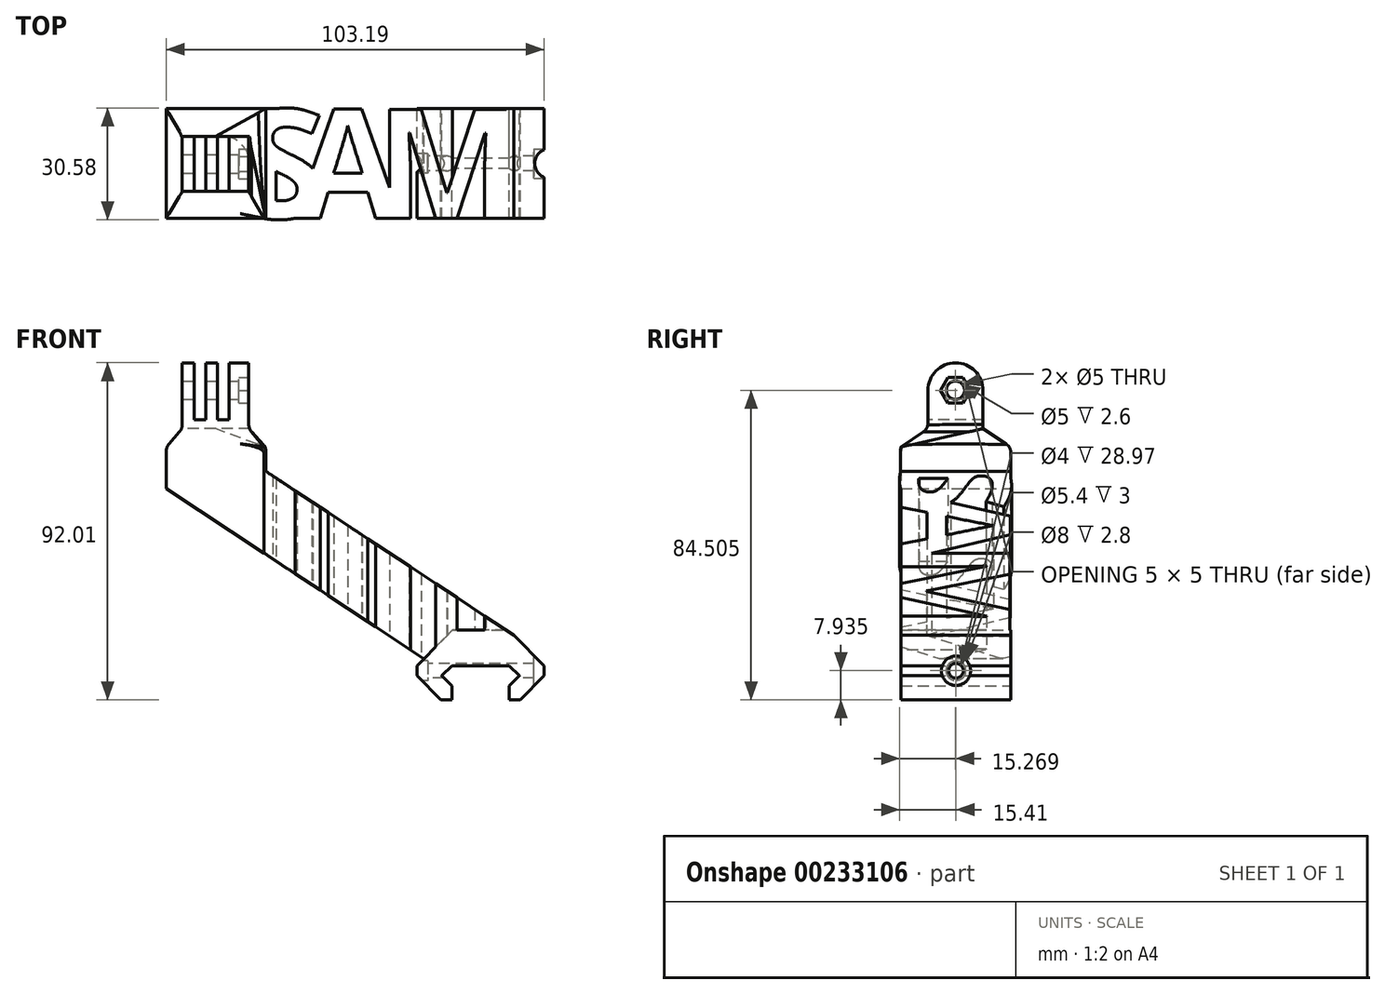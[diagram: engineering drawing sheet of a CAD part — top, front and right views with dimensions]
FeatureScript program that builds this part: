
annotation { "Feature Type Name" : "Feature", "Feature Type Description" : "" }
export const myFeature = defineFeature(function(context is Context, id is Id, definition is map)
    precondition{}
    {
        {
            var Q0;
            Q0=qCreatedBy(makeId("Front.planeOp"),FACE);
            var sketch = newSketch(context, id + "F0", { "sketchPlane" : qUnion([Q0])});
            skLineSegment(sketch, "E0", {"start": v(0, 0) * mm, "end": v(-7.83, 0) * mm, "construction": true});
            skLineSegment(sketch, "E1", {"start": v(-7.83, 0) * mm, "end": v(-7.83, 3.78) * mm});
            skLineSegment(sketch, "E2", {"start": v(-7.84, 3.78) * mm, "end": v(-10.6, 6.55) * mm});
            skLineSegment(sketch, "E3", {"start": v(-10.6, 6.55) * mm, "end": v(-7.83, 9.32) * mm});
            skLineSegment(sketch, "E4", {"start": v(-7.84, 9.32) * mm, "end": v(0, 9.32) * mm});
            skLineSegment(sketch, "E5", {"start": v(0, 9.32) * mm, "end": v(0, 0) * mm, "construction": true});
            skLineSegment(sketch, "E6", {"start": v(-7.83, 9.32) * mm, "end": v(-7.83, 3.78) * mm, "construction": true});
            skLineSegment(sketch, "E7.MirrorCS", {"start": v(7.84, 9.32) * mm, "end": v(0, 9.32) * mm});
            skLineSegment(sketch, "E8.MirrorCS", {"start": v(10.6, 6.55) * mm, "end": v(7.83, 9.32) * mm});
            skLineSegment(sketch, "E9.MirrorCS", {"start": v(7.84, 3.78) * mm, "end": v(10.6, 6.55) * mm});
            skLineSegment(sketch, "E10.MirrorCS", {"start": v(7.83, 0) * mm, "end": v(7.83, 3.78) * mm});
            skLineSegment(sketch, "E11", {"start": v(-10.84, 0) * mm, "end": v(-17.38, 6.55) * mm});
            skLineSegment(sketch, "E12", {"start": v(-17.38, 6.55) * mm, "end": v(-17.38, 9.32) * mm});
            skLineSegment(sketch, "E13", {"start": v(-17.39, 9.32) * mm, "end": v(-7.7, 19) * mm});
            skLineSegment(sketch, "E14", {"start": v(-7.7, 19) * mm, "end": v(0, 19) * mm});
            skLineSegment(sketch, "E15", {"start": v(-10.6, 6.55) * mm, "end": v(-17.38, 6.55) * mm, "construction": true});
            skLineSegment(sketch, "E16", {"start": v(-17.38, 9.32) * mm, "end": v(-7.84, 9.32) * mm, "construction": true});
            skLineSegment(sketch, "E17.MirrorCS", {"start": v(7.7, 19) * mm, "end": v(0, 19) * mm});
            skLineSegment(sketch, "E18.MirrorCS", {"start": v(17.39, 9.32) * mm, "end": v(7.7, 19) * mm});
            skLineSegment(sketch, "E19.MirrorCS", {"start": v(17.38, 6.55) * mm, "end": v(17.38, 9.32) * mm});
            skLineSegment(sketch, "E20.MirrorCS", {"start": v(10.83, 0) * mm, "end": v(17.38, 6.55) * mm});
            skLineSegment(sketch, "E21", {"start": v(-7.83, 0) * mm, "end": v(-10.84, 0) * mm});
            skLineSegment(sketch, "E22", {"start": v(7.83, 0) * mm, "end": v(10.84, 0) * mm});
            skSolve(sketch);
        }
        {
            var Q0;
            Q0=makeQuery(id+"F0.imprint","IMPRINT",FACE,{"disambiguationData":[TD([[makeQuery(id+"F0.imprint","IMPRINT",EDGE,{"derivedFrom":sQuery(id+"F0.wireOp",EDGE,"E1")}),1.0]])]});
            extrude(context, id + "F1", {"entities" : qUnion([Q0]), "depth" : 30 * mm, "offsetDistance" : 25 * mm});
        }
        {
            var Q0;
            Q0=makeQuery(id+"F1.opExtrude","SWEPT_FACE",FACE,{"disambiguationData":[OSD([sQuery(id+"F0.wireOp",EDGE,"E12")])]});
            var sketch = newSketch(context, id + "F2", { "sketchPlane" : qUnion([Q0])});
            skCircle(sketch, "E23", {"center": v(15, 7.94) * mm, "radius": 2 * mm});
            skPoint(sketch, "E23.centerSnap0", {"position": v(15, 6.55) * mm});
            skLineSegment(sketch, "E24", {"start": v(15, 9.32) * mm, "end": v(15, 6.55) * mm, "construction": true});
            skSolve(sketch);
        }
        {
            var Q0;
            Q0=qSketchRegion(id+"F2",true);
            extrude(context, id + "F3", {"entities" : qUnion([Q0]), "operationType" : NewBodyOperationType.REMOVE, "oppositeDirection" : true, "depth" : 61.1 * mm, "offsetDistance" : 25 * mm});
        }
        {
            var Q0;
            {var subQ0=sQuery(id+"F0.wireOp",EDGE,"E13");var subQ1=sQuery(id+"F0.wireOp",EDGE,"E12");var subQ2=sQuery(id+"F0.wireOp",EDGE,"E11");Q0=makeQuery(id+"F3.boolean.opBoolean","SPLIT",FACE,{"disambiguationData":[TD([makeQuery(id+"F1.opExtrude","CAP_FACE",FACE,{"disambiguationData":[OSD([sQuery(id+"F0.wireOp",EDGE,"E1"),sQuery(id+"F0.wireOp",EDGE,"E2"),sQuery(id+"F0.wireOp",EDGE,"E3"),sQuery(id+"F0.wireOp",EDGE,"E4"),sQuery(id+"F0.wireOp",EDGE,"E7.MirrorCS"),sQuery(id+"F0.wireOp",EDGE,"E8.MirrorCS"),sQuery(id+"F0.wireOp",EDGE,"E9.MirrorCS"),sQuery(id+"F0.wireOp",EDGE,"E10.MirrorCS"),subQ2,subQ1,subQ0,sQuery(id+"F0.wireOp",EDGE,"E14"),sQuery(id+"F0.wireOp",EDGE,"E17.MirrorCS"),sQuery(id+"F0.wireOp",EDGE,"E18.MirrorCS"),sQuery(id+"F0.wireOp",EDGE,"E19.MirrorCS"),sQuery(id+"F0.wireOp",EDGE,"E20.MirrorCS"),sQuery(id+"F0.wireOp",EDGE,"E21"),sQuery(id+"F0.wireOp",EDGE,"E22")])],"isStart":false})])],"derivedFrom":makeQuery(id+"F1.opExtrude","SWEPT_FACE",FACE,{"disambiguationData":[OSD([subQ1])]})});}
            var sketch = newSketch(context, id + "F4", { "sketchPlane" : qUnion([Q0])});
            skCircle(sketch, "E25", {"center": v(15, 7.94) * mm, "radius": 2.7 * mm});
            skSolve(sketch);
        }
        {
            var Q0;
            Q0=qSketchRegion(id+"F4",true);
            extrude(context, id + "F5", {"entities" : qUnion([Q0]), "operationType" : NewBodyOperationType.REMOVE, "oppositeDirection" : true, "depth" : 3 * mm, "offsetDistance" : 25 * mm});
        }
        {
            var Q0;
            {var subQ0=sQuery(id+"F0.wireOp",EDGE,"E20.MirrorCS");var subQ1=sQuery(id+"F0.wireOp",EDGE,"E19.MirrorCS");var subQ2=sQuery(id+"F0.wireOp",EDGE,"E18.MirrorCS");Q0=makeQuery(id+"F3.boolean.opBoolean","SPLIT",FACE,{"disambiguationData":[TD([makeQuery(id+"F1.opExtrude","CAP_FACE",FACE,{"disambiguationData":[OSD([sQuery(id+"F0.wireOp",EDGE,"E1"),sQuery(id+"F0.wireOp",EDGE,"E2"),sQuery(id+"F0.wireOp",EDGE,"E3"),sQuery(id+"F0.wireOp",EDGE,"E4"),sQuery(id+"F0.wireOp",EDGE,"E7.MirrorCS"),sQuery(id+"F0.wireOp",EDGE,"E8.MirrorCS"),sQuery(id+"F0.wireOp",EDGE,"E9.MirrorCS"),sQuery(id+"F0.wireOp",EDGE,"E10.MirrorCS"),sQuery(id+"F0.wireOp",EDGE,"E11"),sQuery(id+"F0.wireOp",EDGE,"E12"),sQuery(id+"F0.wireOp",EDGE,"E13"),sQuery(id+"F0.wireOp",EDGE,"E14"),sQuery(id+"F0.wireOp",EDGE,"E17.MirrorCS"),subQ2,subQ1,subQ0,sQuery(id+"F0.wireOp",EDGE,"E21"),sQuery(id+"F0.wireOp",EDGE,"E22")])],"isStart":false})])],"derivedFrom":makeQuery(id+"F1.opExtrude","SWEPT_FACE",FACE,{"disambiguationData":[OSD([subQ1])]})});}
            var sketch = newSketch(context, id + "F6", { "sketchPlane" : qUnion([Q0])});
            skCircle(sketch, "E26", {"center": v(-15, 7.93) * mm, "radius": 4 * mm});
            skSolve(sketch);
        }
        {
            var Q0;
            Q0=qSketchRegion(id+"F6",true);
            extrude(context, id + "F7", {"entities" : qUnion([Q0]), "operationType" : NewBodyOperationType.REMOVE, "oppositeDirection" : true, "depth" : 2.8 * mm, "offsetDistance" : 25 * mm});
        }
        {
            var Q0;
            Q0=makeQuery(id+"F1.opExtrude","SWEPT_FACE",FACE,{"disambiguationData":[OSD([sQuery(id+"F0.wireOp",EDGE,"E14"),sQuery(id+"F0.wireOp",EDGE,"E17.MirrorCS")])]});
            var sketch = newSketch(context, id + "F8", { "sketchPlane" : qUnion([Q0])});
            skText(sketch, "E27", { "text": "M", "fontName": "OpenSans-Bold.ttf"});
            skText(sketch, "E28", { "text": "A", "fontName": "OpenSans-Bold.ttf"});
            skText(sketch, "E29", { "text": "S", "fontName": "OpenSans-Bold.ttf"});
            skLineSegment(sketch, "E30.bottom", {"start": v(-55.8, -30) * mm, "end": v(-85.8, -30) * mm});
            skLineSegment(sketch, "E30.top", {"start": v(-55.8, 0) * mm, "end": v(-85.8, 0) * mm});
            skLineSegment(sketch, "E30.left", {"start": v(-55.8, -30) * mm, "end": v(-55.8, 0) * mm});
            skLineSegment(sketch, "E30.right", {"start": v(-85.8, -30) * mm, "end": v(-85.8, 0) * mm});
            const initialGuessF8  = {"E27": [-0.02854, -0.03, 1, 0, 0.03], "E28": [-0.0506, -0.03, 1, 0, 0.03], "E29": [-0.0652, -0.03, 1, 0, 0.03]};
            skSetInitialGuess(sketch, initialGuessF8);
            skSolve(sketch);
        }
        {
            var Q0;
            {var subQ12=sQuery(id+"F8.wireOp",EDGE,"E29.sketch_text.stroke-3");Q0=makeQuery(id+"F8.imprint","IMPRINT",FACE,{"disambiguationData":[TD([[makeQuery(id+"F8.imprint","IMPRINT",EDGE,{"derivedFrom":subQ12}),1.0]])]});}
            var Q1;
            {var subQ9=sQuery(id+"F8.wireOp",EDGE,"E29.sketch_text.stroke-11");Q1=makeQuery(id+"F8.imprint","IMPRINT",FACE,{"disambiguationData":[TD([[makeQuery(id+"F8.imprint","IMPRINT",EDGE,{"derivedFrom":subQ9}),-1.0]])]});}
            var Q2;
            {var subQ0=sQuery(id+"F8.wireOp",EDGE,"E29.sketch_text.stroke-16");Q2=makeQuery(id+"F8.imprint","IMPRINT",FACE,{"disambiguationData":[TD([[makeQuery(id+"F8.imprint","IMPRINT",EDGE,{"derivedFrom":subQ0}),-1.0]])]});}
            var Q3;
            {var subQ10=sQuery(id+"F8.wireOp",EDGE,"E29.sketch_text.stroke-6");Q3=makeQuery(id+"F8.imprint","IMPRINT",FACE,{"disambiguationData":[TD([[makeQuery(id+"F8.imprint","IMPRINT",EDGE,{"derivedFrom":subQ10}),-1.0]])]});}
            var Q4;
            {var subQ6=sQuery(id+"F8.wireOp",EDGE,"E29.sketch_text.stroke-3");Q4=makeQuery(id+"F8.imprint","IMPRINT",FACE,{"disambiguationData":[TD([[makeQuery(id+"F8.imprint","IMPRINT",EDGE,{"derivedFrom":subQ6}),-1.0]])]});}
            var Q5;
            {var subQ1=sQuery(id+"F8.wireOp",EDGE,"E29.sketch_text.stroke-0");Q5=makeQuery(id+"F8.imprint","IMPRINT",FACE,{"disambiguationData":[TD([[makeQuery(id+"F8.imprint","IMPRINT",EDGE,{"derivedFrom":subQ1}),-1.0]])]});}
            var Q6;
            {var subQ13=sQuery(id+"F8.wireOp",EDGE,"E28.sketch_text.stroke-0");Q6=makeQuery(id+"F8.imprint","IMPRINT",FACE,{"disambiguationData":[TD([[makeQuery(id+"F8.imprint","IMPRINT",EDGE,{"derivedFrom":subQ13}),-1.0]])]});}
            var Q7;
            {var subQ9=sQuery(id+"F8.wireOp",EDGE,"E27.sketch_text.stroke-0");Q7=makeQuery(id+"F8.imprint","IMPRINT",FACE,{"disambiguationData":[TD([[makeQuery(id+"F8.imprint","IMPRINT",EDGE,{"derivedFrom":subQ9}),-1.0]])]});}
            var Q8;
            {var subQ7=sQuery(id+"F8.wireOp",EDGE,"E27.sketch_text.stroke-10");Q8=makeQuery(id+"F8.imprint","IMPRINT",FACE,{"disambiguationData":[TD([[makeQuery(id+"F8.imprint","IMPRINT",EDGE,{"derivedFrom":subQ7}),-1.0]])]});}
            var Q9;
            {var subQ0=sQuery(id+"F8.wireOp",EDGE,"E28.sketch_text.stroke-7");var subQ1=sQuery(id+"F8.wireOp",EDGE,"E27.sketch_text.stroke-5");var subQ2=makeQuery(id+"F8.imprint","INTERSECT",VERTEX,{"derivedFrom":[subQ1,subQ0]});Q9=makeQuery(id+"F8.imprint","IMPRINT",FACE,{"disambiguationData":[TD([[makeQuery(id+"F8.imprint","IMPRINT",EDGE,{"disambiguationData":[TD([[subQ2,-1.0]])],"derivedFrom":subQ1}),-1.0]])]});}
            extrude(context, id + "F9", {"entities" : qUnion([Q0, Q1, Q2, Q3, Q4, Q5, Q6, Q7, Q8, Q9]), "operationType" : NewBodyOperationType.ADD, "depth" : 50 * mm, "offsetDistance" : 25 * mm});
        }
        {
            var Q0;
            Q0=makeQuery(id+"F9.opExtrude","CAP_FACE",FACE,{"disambiguationData":[OSD([sQuery(id+"F8.wireOp",EDGE,"E27.sketch_text.stroke-0"),sQuery(id+"F8.wireOp",EDGE,"E27.sketch_text.stroke-1"),sQuery(id+"F8.wireOp",EDGE,"E27.sketch_text.stroke-2"),sQuery(id+"F8.wireOp",EDGE,"E27.sketch_text.stroke-3"),sQuery(id+"F8.wireOp",EDGE,"E27.sketch_text.stroke-4"),sQuery(id+"F8.wireOp",EDGE,"E27.sketch_text.stroke-5"),sQuery(id+"F8.wireOp",EDGE,"E27.sketch_text.stroke-6"),sQuery(id+"F8.wireOp",EDGE,"E27.sketch_text.stroke-7"),sQuery(id+"F8.wireOp",EDGE,"E27.sketch_text.stroke-8"),sQuery(id+"F8.wireOp",EDGE,"E27.sketch_text.stroke-9"),sQuery(id+"F8.wireOp",EDGE,"E27.sketch_text.stroke-10"),sQuery(id+"F8.wireOp",EDGE,"E27.sketch_text.stroke-11"),sQuery(id+"F8.wireOp",EDGE,"E27.sketch_text.stroke-12"),sQuery(id+"F8.wireOp",EDGE,"E27.sketch_text.stroke-13"),sQuery(id+"F8.wireOp",EDGE,"E27.sketch_text.stroke-14"),sQuery(id+"F8.wireOp",EDGE,"E27.sketch_text.stroke-15"),sQuery(id+"F8.wireOp",EDGE,"E27.sketch_text.stroke-16"),sQuery(id+"F8.wireOp",EDGE,"E27.sketch_text.stroke-17"),sQuery(id+"F8.wireOp",EDGE,"E27.sketch_text.stroke-18"),sQuery(id+"F8.wireOp",EDGE,"E28.sketch_text.stroke-0"),sQuery(id+"F8.wireOp",EDGE,"E28.sketch_text.stroke-1"),sQuery(id+"F8.wireOp",EDGE,"E28.sketch_text.stroke-2"),sQuery(id+"F8.wireOp",EDGE,"E28.sketch_text.stroke-3"),sQuery(id+"F8.wireOp",EDGE,"E28.sketch_text.stroke-4"),sQuery(id+"F8.wireOp",EDGE,"E28.sketch_text.stroke-5"),sQuery(id+"F8.wireOp",EDGE,"E28.sketch_text.stroke-6"),sQuery(id+"F8.wireOp",EDGE,"E28.sketch_text.stroke-7"),sQuery(id+"F8.wireOp",EDGE,"E28.sketch_text.stroke-8"),sQuery(id+"F8.wireOp",EDGE,"E28.sketch_text.stroke-9"),sQuery(id+"F8.wireOp",EDGE,"E28.sketch_text.stroke-10"),sQuery(id+"F8.wireOp",EDGE,"E28.sketch_text.stroke-11"),sQuery(id+"F8.wireOp",EDGE,"E29.sketch_text.stroke-1"),sQuery(id+"F8.wireOp",EDGE,"E29.sketch_text.stroke-2"),sQuery(id+"F8.wireOp",EDGE,"E29.sketch_text.stroke-5"),sQuery(id+"F8.wireOp",EDGE,"E29.sketch_text.stroke-6"),sQuery(id+"F8.wireOp",EDGE,"E29.sketch_text.stroke-7"),sQuery(id+"F8.wireOp",EDGE,"E29.sketch_text.stroke-8"),sQuery(id+"F8.wireOp",EDGE,"E29.sketch_text.stroke-9"),sQuery(id+"F8.wireOp",EDGE,"E29.sketch_text.stroke-10"),sQuery(id+"F8.wireOp",EDGE,"E29.sketch_text.stroke-15"),sQuery(id+"F8.wireOp",EDGE,"E29.sketch_text.stroke-16"),sQuery(id+"F8.wireOp",EDGE,"E29.sketch_text.stroke-17"),sQuery(id+"F8.wireOp",EDGE,"E29.sketch_text.stroke-18"),sQuery(id+"F8.wireOp",EDGE,"E29.sketch_text.stroke-19"),sQuery(id+"F8.wireOp",EDGE,"E29.sketch_text.stroke-20"),sQuery(id+"F8.wireOp",EDGE,"E29.sketch_text.stroke-21"),sQuery(id+"F8.wireOp",EDGE,"E29.sketch_text.stroke-22"),sQuery(id+"F8.wireOp",EDGE,"E29.sketch_text.stroke-23"),sQuery(id+"F8.wireOp",EDGE,"E29.sketch_text.stroke-24"),sQuery(id+"F8.wireOp",EDGE,"E29.sketch_text.stroke-25"),sQuery(id+"F8.wireOp",EDGE,"E29.sketch_text.stroke-26"),sQuery(id+"F8.wireOp",EDGE,"E30.bottom"),sQuery(id+"F8.wireOp",EDGE,"E30.top"),sQuery(id+"F8.wireOp",EDGE,"E30.left"),sQuery(id+"F8.wireOp",EDGE,"E30.right")])],"isStart":true});
            extrude(context, id + "F10", {"entities" : qUnion([Q0]), "operationType" : NewBodyOperationType.ADD, "flatOperationType" : FlatOperationType.REMOVE, "depth" : 7.7 * mm, "offsetDistance" : 25 * mm, "domain" : OperationDomain.MODEL});
        }
        {
            var Q0;
            {var subQ0=sQuery(id+"F8.wireOp",EDGE,"E27.sketch_text.stroke-18");Q0=makeQuery(id+"F10.boolean.opBoolean","MERGE",FACE,{"derivedFrom":[makeQuery(id+"F9.boolean.opBoolean","MERGE",FACE,{"derivedFrom":[makeQuery(id+"F1.opExtrude","CAP_FACE",FACE,{"disambiguationData":[OSD([sQuery(id+"F0.wireOp",EDGE,"E1"),sQuery(id+"F0.wireOp",EDGE,"E2"),sQuery(id+"F0.wireOp",EDGE,"E3"),sQuery(id+"F0.wireOp",EDGE,"E4"),sQuery(id+"F0.wireOp",EDGE,"E7.MirrorCS"),sQuery(id+"F0.wireOp",EDGE,"E8.MirrorCS"),sQuery(id+"F0.wireOp",EDGE,"E9.MirrorCS"),sQuery(id+"F0.wireOp",EDGE,"E10.MirrorCS"),sQuery(id+"F0.wireOp",EDGE,"E11"),sQuery(id+"F0.wireOp",EDGE,"E12"),sQuery(id+"F0.wireOp",EDGE,"E13"),sQuery(id+"F0.wireOp",EDGE,"E14"),sQuery(id+"F0.wireOp",EDGE,"E17.MirrorCS"),sQuery(id+"F0.wireOp",EDGE,"E18.MirrorCS"),sQuery(id+"F0.wireOp",EDGE,"E19.MirrorCS"),sQuery(id+"F0.wireOp",EDGE,"E20.MirrorCS"),sQuery(id+"F0.wireOp",EDGE,"E21"),sQuery(id+"F0.wireOp",EDGE,"E22")])],"isStart":false}),makeQuery(id+"F9.opExtrude","SWEPT_FACE",FACE,{"disambiguationData":[OSD([sQuery(id+"F8.wireOp",EDGE,"E27.sketch_text.stroke-12")])]}),makeQuery(id+"F9.opExtrude","SWEPT_FACE",FACE,{"disambiguationData":[OSD([subQ0])]})]}),makeQuery(id+"F10.opExtrude","SWEPT_FACE",FACE,{"disambiguationData":[OSD([subQ0])]})]});}
            var sketch = newSketch(context, id + "F11", { "sketchPlane" : qUnion([Q0])});
            skLineSegment(sketch, "E31", {"start": v(-15.5, 11.21) * mm, "end": v(-89.99, 60.43) * mm});
            skLineSegment(sketch, "E32", {"start": v(-89.99, 60.43) * mm, "end": v(-97.13, 11.21) * mm});
            skLineSegment(sketch, "E33", {"start": v(-97.13, 11.21) * mm, "end": v(-15.5, 11.21) * mm});
            skLineSegment(sketch, "E34", {"start": v(7, 19) * mm, "end": v(-58.66, 62.39) * mm});
            skLineSegment(sketch, "E35", {"start": v(-58.66, 62.39) * mm, "end": v(-58.66, 76.31) * mm});
            skLineSegment(sketch, "E36", {"start": v(-58.66, 76.31) * mm, "end": v(20.15, 71.26) * mm});
            skLineSegment(sketch, "E37", {"start": v(20.15, 71.26) * mm, "end": v(7, 19) * mm});
            skLineSegment(sketch, "E38", {"start": v(7, 19) * mm, "end": v(23.58, 8.05) * mm});
            skLineSegment(sketch, "E39", {"start": v(23.58, 8.05) * mm, "end": v(25.66, 13.08) * mm});
            skLineSegment(sketch, "E40", {"start": v(25.66, 13.08) * mm, "end": v(11.19, 20.33) * mm});
            skLineSegment(sketch, "E41", {"start": v(11.19, 20.33) * mm, "end": v(7.88, 22.52) * mm});
            skSolve(sketch);
        }
        {
            var Q0;
            Q0=makeQuery(id+"F11.imprint","IMPRINT",FACE,{"disambiguationData":[TD([[makeQuery(id+"F11.imprint","IMPRINT",EDGE,{"derivedFrom":sQuery(id+"F11.wireOp",EDGE,"E31")}),1.0]])]});
            var Q1;
            {var subQ11=sQuery(id+"F11.wireOp",EDGE,"E35");Q1=makeQuery(id+"F11.imprint","IMPRINT",FACE,{"disambiguationData":[TD([[makeQuery(id+"F11.imprint","IMPRINT",EDGE,{"derivedFrom":subQ11}),-1.0]])]});}
            var Q2;
            {var subQ5=sQuery(id+"F8.wireOp",EDGE,"E27.sketch_text.stroke-12");var subQ9=makeQuery(id+"F9.opExtrude","CAP_EDGE",EDGE,{"disambiguationData":[OSD([subQ5])],"isStart":false});Q2=makeQuery(id+"F11.imprint","IMPRINT",FACE,{"disambiguationData":[TD([[makeQuery(id+"F11.imprint","IMPRINT",EDGE,{"derivedFrom":subQ9}),1.0]])]});}
            var Q3;
            {var subQ1=sQuery(id+"F8.wireOp",EDGE,"E27.sketch_text.stroke-18");var subQ7=makeQuery(id+"F9.opExtrude","CAP_EDGE",EDGE,{"disambiguationData":[OSD([subQ1])],"isStart":false});Q3=makeQuery(id+"F11.imprint","IMPRINT",FACE,{"disambiguationData":[TD([[makeQuery(id+"F11.imprint","IMPRINT",EDGE,{"derivedFrom":subQ7}),1.0]])]});}
            extrude(context, id + "F12", {"entities" : qUnion([Q0, Q1, Q2, Q3]), "operationType" : NewBodyOperationType.REMOVE, "flatOperationType" : FlatOperationType.REMOVE, "oppositeDirection" : true, "depth" : 85 * mm, "offsetDistance" : 25 * mm, "domain" : OperationDomain.MODEL});
        }
        {
            var Q0;
            Q0=makeQuery(id+"F11.imprint","IMPRINT",FACE,{"disambiguationData":[TD([[makeQuery(id+"F11.imprint","IMPRINT",EDGE,{"derivedFrom":sQuery(id+"F11.wireOp",EDGE,"E31")}),1.0]])]});
            var Q1;
            {var subQ11=sQuery(id+"F11.wireOp",EDGE,"E35");Q1=makeQuery(id+"F11.imprint","IMPRINT",FACE,{"disambiguationData":[TD([[makeQuery(id+"F11.imprint","IMPRINT",EDGE,{"derivedFrom":subQ11}),-1.0]])]});}
            extrude(context, id + "F13", {"entities" : qUnion([Q0, Q1]), "operationType" : NewBodyOperationType.REMOVE, "depth" : 25 * mm, "offsetDistance" : 25 * mm});
        }
        {
            var Q0;
            {var subQ2=sQuery(id+"F0.wireOp",EDGE,"E18.MirrorCS");var subQ3=sQuery(id+"F0.wireOp",EDGE,"E17.MirrorCS");var subQ4=sQuery(id+"F0.wireOp",EDGE,"E14");var subQ6=makeQuery(id+"F9.boolean.opBoolean","SPLIT",EDGE,{"disambiguationData":[TD([makeQuery(id+"F1.opExtrude","SWEPT_FACE",FACE,{"disambiguationData":[OSD([subQ2])]})])],"derivedFrom":makeQuery(id+"F1.opExtrude","CAP_EDGE",EDGE,{"disambiguationData":[OSD([subQ4,subQ3])],"isStart":false})});Q0=makeQuery(id+"F11.imprint","IMPRINT",FACE,{"disambiguationData":[TD([[makeQuery(id+"F11.imprint","IMPRINT",EDGE,{"derivedFrom":subQ6}),1.0]])]});}
            extrude(context, id + "F14", {"entities" : qUnion([Q0]), "operationType" : NewBodyOperationType.REMOVE, "oppositeDirection" : true, "depth" : 37.4 * mm, "offsetDistance" : 25 * mm});
        }
        {
            var Q0;
            Q0=makeQuery(id+"F9.opExtrude","CAP_FACE",FACE,{"disambiguationData":[OSD([sQuery(id+"F8.wireOp",EDGE,"E27.sketch_text.stroke-0"),sQuery(id+"F8.wireOp",EDGE,"E27.sketch_text.stroke-1"),sQuery(id+"F8.wireOp",EDGE,"E27.sketch_text.stroke-2"),sQuery(id+"F8.wireOp",EDGE,"E27.sketch_text.stroke-3"),sQuery(id+"F8.wireOp",EDGE,"E27.sketch_text.stroke-4"),sQuery(id+"F8.wireOp",EDGE,"E27.sketch_text.stroke-5"),sQuery(id+"F8.wireOp",EDGE,"E27.sketch_text.stroke-6"),sQuery(id+"F8.wireOp",EDGE,"E27.sketch_text.stroke-7"),sQuery(id+"F8.wireOp",EDGE,"E27.sketch_text.stroke-8"),sQuery(id+"F8.wireOp",EDGE,"E27.sketch_text.stroke-9"),sQuery(id+"F8.wireOp",EDGE,"E27.sketch_text.stroke-10"),sQuery(id+"F8.wireOp",EDGE,"E27.sketch_text.stroke-11"),sQuery(id+"F8.wireOp",EDGE,"E27.sketch_text.stroke-12"),sQuery(id+"F8.wireOp",EDGE,"E27.sketch_text.stroke-13"),sQuery(id+"F8.wireOp",EDGE,"E27.sketch_text.stroke-14"),sQuery(id+"F8.wireOp",EDGE,"E27.sketch_text.stroke-15"),sQuery(id+"F8.wireOp",EDGE,"E27.sketch_text.stroke-16"),sQuery(id+"F8.wireOp",EDGE,"E27.sketch_text.stroke-17"),sQuery(id+"F8.wireOp",EDGE,"E27.sketch_text.stroke-18"),sQuery(id+"F8.wireOp",EDGE,"E28.sketch_text.stroke-0"),sQuery(id+"F8.wireOp",EDGE,"E28.sketch_text.stroke-1"),sQuery(id+"F8.wireOp",EDGE,"E28.sketch_text.stroke-2"),sQuery(id+"F8.wireOp",EDGE,"E28.sketch_text.stroke-3"),sQuery(id+"F8.wireOp",EDGE,"E28.sketch_text.stroke-4"),sQuery(id+"F8.wireOp",EDGE,"E28.sketch_text.stroke-5"),sQuery(id+"F8.wireOp",EDGE,"E28.sketch_text.stroke-6"),sQuery(id+"F8.wireOp",EDGE,"E28.sketch_text.stroke-7"),sQuery(id+"F8.wireOp",EDGE,"E28.sketch_text.stroke-8"),sQuery(id+"F8.wireOp",EDGE,"E28.sketch_text.stroke-9"),sQuery(id+"F8.wireOp",EDGE,"E28.sketch_text.stroke-10"),sQuery(id+"F8.wireOp",EDGE,"E28.sketch_text.stroke-11"),sQuery(id+"F8.wireOp",EDGE,"E29.sketch_text.stroke-1"),sQuery(id+"F8.wireOp",EDGE,"E29.sketch_text.stroke-2"),sQuery(id+"F8.wireOp",EDGE,"E29.sketch_text.stroke-5"),sQuery(id+"F8.wireOp",EDGE,"E29.sketch_text.stroke-6"),sQuery(id+"F8.wireOp",EDGE,"E29.sketch_text.stroke-7"),sQuery(id+"F8.wireOp",EDGE,"E29.sketch_text.stroke-8"),sQuery(id+"F8.wireOp",EDGE,"E29.sketch_text.stroke-9"),sQuery(id+"F8.wireOp",EDGE,"E29.sketch_text.stroke-10"),sQuery(id+"F8.wireOp",EDGE,"E29.sketch_text.stroke-15"),sQuery(id+"F8.wireOp",EDGE,"E29.sketch_text.stroke-16"),sQuery(id+"F8.wireOp",EDGE,"E29.sketch_text.stroke-17"),sQuery(id+"F8.wireOp",EDGE,"E29.sketch_text.stroke-18"),sQuery(id+"F8.wireOp",EDGE,"E29.sketch_text.stroke-19"),sQuery(id+"F8.wireOp",EDGE,"E29.sketch_text.stroke-20"),sQuery(id+"F8.wireOp",EDGE,"E29.sketch_text.stroke-21"),sQuery(id+"F8.wireOp",EDGE,"E29.sketch_text.stroke-22"),sQuery(id+"F8.wireOp",EDGE,"E29.sketch_text.stroke-23"),sQuery(id+"F8.wireOp",EDGE,"E29.sketch_text.stroke-24"),sQuery(id+"F8.wireOp",EDGE,"E29.sketch_text.stroke-25"),sQuery(id+"F8.wireOp",EDGE,"E29.sketch_text.stroke-26"),sQuery(id+"F8.wireOp",EDGE,"E30.bottom"),sQuery(id+"F8.wireOp",EDGE,"E30.top"),sQuery(id+"F8.wireOp",EDGE,"E30.left"),sQuery(id+"F8.wireOp",EDGE,"E30.right")])],"isStart":false});
            cPlane(context, id + "F15", {"entities" : qUnion([Q0]), "cplaneType" : CPlaneType.OFFSET, "offset" : 5 * mm, "width" : 150 * mm, "height" : 150 * mm});
        }
        {
            var Q0;
            Q0=makeQuery(id+"F9.opExtrude","CAP_FACE",FACE,{"disambiguationData":[OSD([sQuery(id+"F8.wireOp",EDGE,"E27.sketch_text.stroke-0"),sQuery(id+"F8.wireOp",EDGE,"E27.sketch_text.stroke-1"),sQuery(id+"F8.wireOp",EDGE,"E27.sketch_text.stroke-2"),sQuery(id+"F8.wireOp",EDGE,"E27.sketch_text.stroke-3"),sQuery(id+"F8.wireOp",EDGE,"E27.sketch_text.stroke-4"),sQuery(id+"F8.wireOp",EDGE,"E27.sketch_text.stroke-5"),sQuery(id+"F8.wireOp",EDGE,"E27.sketch_text.stroke-6"),sQuery(id+"F8.wireOp",EDGE,"E27.sketch_text.stroke-7"),sQuery(id+"F8.wireOp",EDGE,"E27.sketch_text.stroke-8"),sQuery(id+"F8.wireOp",EDGE,"E27.sketch_text.stroke-9"),sQuery(id+"F8.wireOp",EDGE,"E27.sketch_text.stroke-10"),sQuery(id+"F8.wireOp",EDGE,"E27.sketch_text.stroke-11"),sQuery(id+"F8.wireOp",EDGE,"E27.sketch_text.stroke-12"),sQuery(id+"F8.wireOp",EDGE,"E27.sketch_text.stroke-13"),sQuery(id+"F8.wireOp",EDGE,"E27.sketch_text.stroke-14"),sQuery(id+"F8.wireOp",EDGE,"E27.sketch_text.stroke-15"),sQuery(id+"F8.wireOp",EDGE,"E27.sketch_text.stroke-16"),sQuery(id+"F8.wireOp",EDGE,"E27.sketch_text.stroke-17"),sQuery(id+"F8.wireOp",EDGE,"E27.sketch_text.stroke-18"),sQuery(id+"F8.wireOp",EDGE,"E28.sketch_text.stroke-0"),sQuery(id+"F8.wireOp",EDGE,"E28.sketch_text.stroke-1"),sQuery(id+"F8.wireOp",EDGE,"E28.sketch_text.stroke-2"),sQuery(id+"F8.wireOp",EDGE,"E28.sketch_text.stroke-3"),sQuery(id+"F8.wireOp",EDGE,"E28.sketch_text.stroke-4"),sQuery(id+"F8.wireOp",EDGE,"E28.sketch_text.stroke-5"),sQuery(id+"F8.wireOp",EDGE,"E28.sketch_text.stroke-6"),sQuery(id+"F8.wireOp",EDGE,"E28.sketch_text.stroke-7"),sQuery(id+"F8.wireOp",EDGE,"E28.sketch_text.stroke-8"),sQuery(id+"F8.wireOp",EDGE,"E28.sketch_text.stroke-9"),sQuery(id+"F8.wireOp",EDGE,"E28.sketch_text.stroke-10"),sQuery(id+"F8.wireOp",EDGE,"E28.sketch_text.stroke-11"),sQuery(id+"F8.wireOp",EDGE,"E29.sketch_text.stroke-1"),sQuery(id+"F8.wireOp",EDGE,"E29.sketch_text.stroke-2"),sQuery(id+"F8.wireOp",EDGE,"E29.sketch_text.stroke-5"),sQuery(id+"F8.wireOp",EDGE,"E29.sketch_text.stroke-6"),sQuery(id+"F8.wireOp",EDGE,"E29.sketch_text.stroke-7"),sQuery(id+"F8.wireOp",EDGE,"E29.sketch_text.stroke-8"),sQuery(id+"F8.wireOp",EDGE,"E29.sketch_text.stroke-9"),sQuery(id+"F8.wireOp",EDGE,"E29.sketch_text.stroke-10"),sQuery(id+"F8.wireOp",EDGE,"E29.sketch_text.stroke-15"),sQuery(id+"F8.wireOp",EDGE,"E29.sketch_text.stroke-16"),sQuery(id+"F8.wireOp",EDGE,"E29.sketch_text.stroke-17"),sQuery(id+"F8.wireOp",EDGE,"E29.sketch_text.stroke-18"),sQuery(id+"F8.wireOp",EDGE,"E29.sketch_text.stroke-19"),sQuery(id+"F8.wireOp",EDGE,"E29.sketch_text.stroke-20"),sQuery(id+"F8.wireOp",EDGE,"E29.sketch_text.stroke-21"),sQuery(id+"F8.wireOp",EDGE,"E29.sketch_text.stroke-22"),sQuery(id+"F8.wireOp",EDGE,"E29.sketch_text.stroke-23"),sQuery(id+"F8.wireOp",EDGE,"E29.sketch_text.stroke-24"),sQuery(id+"F8.wireOp",EDGE,"E29.sketch_text.stroke-25"),sQuery(id+"F8.wireOp",EDGE,"E29.sketch_text.stroke-26"),sQuery(id+"F8.wireOp",EDGE,"E30.bottom"),sQuery(id+"F8.wireOp",EDGE,"E30.top"),sQuery(id+"F8.wireOp",EDGE,"E30.left"),sQuery(id+"F8.wireOp",EDGE,"E30.right")])],"isStart":false});
            var sketch = newSketch(context, id + "F16", { "sketchPlane" : qUnion([Q0])});
            skLineSegment(sketch, "E42", {"start": v(-85.8, 0) * mm, "end": v(-59.16, -30) * mm, "construction": true});
            skLineSegment(sketch, "E43", {"start": v(-58.66, 0) * mm, "end": v(-85.8, -30) * mm, "construction": true});
            skLineSegment(sketch, "E44", {"start": v(-72.35, -15.14) * mm, "end": v(-72.35, -30) * mm, "construction": true});
            skSolve(sketch);
        }
        {
            var Q0;
            Q0=qCreatedBy(id+"F15.planeOp",FACE);
            var sketch = newSketch(context, id + "F17", { "sketchPlane" : qUnion([Q0])});
            skLineSegment(sketch, "E45.bottom", {"start": v(-63.28, -22.64) * mm, "end": v(-81.43, -22.64) * mm});
            skLineSegment(sketch, "E45.top", {"start": v(-63.28, -7.64) * mm, "end": v(-81.43, -7.64) * mm});
            skLineSegment(sketch, "E45.left", {"start": v(-63.28, -22.64) * mm, "end": v(-63.28, -7.64) * mm});
            skLineSegment(sketch, "E45.right", {"start": v(-81.43, -22.64) * mm, "end": v(-81.43, -7.64) * mm});
            skPoint(sketch, "E45.middle", {"position": v(-72.35, -15.14) * mm});
            skSolve(sketch);
        }
        {
            var Q0;
            {var subQ3=sQuery(id+"F8.wireOp",EDGE,"E30.bottom");Q0=makeQuery(id+"F16.imprint","IMPRINT",FACE,{"disambiguationData":[TD([[makeQuery(id+"F16.imprint","IMPRINT",EDGE,{"derivedFrom":makeQuery(id+"F9.opExtrude","CAP_EDGE",EDGE,{"disambiguationData":[OSD([subQ3])],"isStart":false})}),-1.0]])]});}
            var Q1;
            Q1=makeQuery(id+"F17.imprint","IMPRINT",FACE,{"disambiguationData":[TD([[makeQuery(id+"F17.imprint","IMPRINT",EDGE,{"derivedFrom":sQuery(id+"F17.wireOp",EDGE,"E45.bottom")}),-1.0]])]});
            loft(context, id + "F18", {"operationType" : NewBodyOperationType.ADD, "sheetProfilesArray" : [{ "sheetProfileEntities" : qUnion([Q0]) }, { "sheetProfileEntities" : qUnion([Q1]) }]});
        }
        {
            var Q0;
            Q0=makeQuery(id+"F18.opLoft","CAP_FACE",FACE,{"disambiguationData":[OSD([makeQuery(id+"F17.imprint","IMPRINT",FACE,{"disambiguationData":[TD([[makeQuery(id+"F17.imprint","IMPRINT",EDGE,{"derivedFrom":sQuery(id+"F17.wireOp",EDGE,"E45.bottom")}),-1.0]])]})])],"isStart":true});
            extrude(context, id + "F19", {"entities" : qUnion([Q0]), "operationType" : NewBodyOperationType.ADD, "depth" : 18 * mm, "offsetDistance" : 25 * mm});
        }
        {
            var Q0;
            Q0=makeQuery(id+"F19.opExtrude","SWEPT_FACE",FACE,{"disambiguationData":[OSD([sQuery(id+"F8.wireOp",EDGE,"E30.bottom"),sQuery(id+"F8.wireOp",EDGE,"E30.right"),sQuery(id+"F17.wireOp",EDGE,"E45.bottom"),sQuery(id+"F17.wireOp",EDGE,"E45.left"),sQuery(id+"F17.wireOp",EDGE,"E45.right")])]});
            var sketch = newSketch(context, id + "F20", { "sketchPlane" : qUnion([Q0])});
            skLineSegment(sketch, "E46", {"start": v(-78.23, 92) * mm, "end": v(-78.23, 76.5) * mm});
            skLineSegment(sketch, "E47", {"start": v(-78.23, 76.5) * mm, "end": v(-75.03, 76.5) * mm});
            skLineSegment(sketch, "E48", {"start": v(-75.03, 76.5) * mm, "end": v(-75.03, 92) * mm});
            skLineSegment(sketch, "E49", {"start": v(-71.83, 92) * mm, "end": v(-71.83, 76.5) * mm});
            skLineSegment(sketch, "E50", {"start": v(-71.83, 76.5) * mm, "end": v(-68.63, 76.5) * mm});
            skLineSegment(sketch, "E51", {"start": v(-68.63, 76.5) * mm, "end": v(-68.63, 92) * mm});
            skLineSegment(sketch, "E52", {"start": v(-75.03, 92) * mm, "end": v(-71.83, 92) * mm, "construction": true});
            skLineSegment(sketch, "E53", {"start": v(-78.23, 92) * mm, "end": v(-81.43, 92) * mm, "construction": true});
            skLineSegment(sketch, "E54", {"start": v(-78.23, 92) * mm, "end": v(-75.03, 92) * mm});
            skLineSegment(sketch, "E55", {"start": v(-71.83, 92) * mm, "end": v(-68.63, 92) * mm});
            skSolve(sketch);
        }
        {
            var Q0;
            Q0=makeQuery(id+"F20.imprint","IMPRINT",FACE,{"disambiguationData":[TD([[makeQuery(id+"F20.imprint","IMPRINT",EDGE,{"derivedFrom":sQuery(id+"F20.wireOp",EDGE,"E46")}),1.0]])]});
            var Q1;
            Q1=makeQuery(id+"F20.imprint","IMPRINT",FACE,{"disambiguationData":[TD([[makeQuery(id+"F20.imprint","IMPRINT",EDGE,{"derivedFrom":sQuery(id+"F20.wireOp",EDGE,"E49")}),1.0]])]});
            extrude(context, id + "F21", {"entities" : qUnion([Q0, Q1]), "operationType" : NewBodyOperationType.REMOVE, "oppositeDirection" : true, "depth" : 15 * mm, "offsetDistance" : 25 * mm});
        }
        {
            var Q0;
            Q0=makeQuery(id+"F19.opExtrude","SWEPT_FACE",FACE,{"disambiguationData":[OSD([sQuery(id+"F17.wireOp",EDGE,"E45.bottom"),sQuery(id+"F17.wireOp",EDGE,"E45.top"),sQuery(id+"F17.wireOp",EDGE,"E45.left")])]});
            var sketch = newSketch(context, id + "F22", { "sketchPlane" : qUnion([Q0])});
            skLineSegment(sketch, "E56", {"start": v(-15.14, 92) * mm, "end": v(-15.14, 84.5) * mm, "construction": true});
            skLineSegment(sketch, "E57", {"start": v(-15.14, 84.5) * mm, "end": v(-22.64, 84.5) * mm, "construction": true});
            skLineSegment(sketch, "E58", {"start": v(-15.14, 84.5) * mm, "end": v(-7.64, 84.5) * mm, "construction": true});
            skArc(sketch, "E59", {"start": v(-7.64, 84.5) * mm, "mid": v(-15.14, 92) * mm, "end": v(-22.64, 84.5) * mm});
            skCircle(sketch, "E60", {"center": v(-15.14, 84.5) * mm, "radius": 2.5 * mm});
            skSolve(sketch);
        }
        {
            var Q0;
            {var subQ0=sQuery(id+"F22.wireOp",EDGE,"E59");var subQ1=sQuery(id+"F17.wireOp",EDGE,"E45.left");var subQ2=sQuery(id+"F17.wireOp",EDGE,"E45.bottom");var subQ3=makeQuery(id+"F19.opExtrude","SWEPT_EDGE",EDGE,{"disambiguationData":[OSD([subQ2,subQ1])]});var subQ4=makeQuery(id+"F22.imprint","INTERSECT",VERTEX,{"derivedFrom":[subQ3,subQ0]});Q0=makeQuery(id+"F22.imprint","IMPRINT",FACE,{"disambiguationData":[TD([[makeQuery(id+"F22.imprint","IMPRINT",EDGE,{"disambiguationData":[TD([[subQ4,1.0]])],"derivedFrom":subQ0}),-1.0]])]});}
            var Q1;
            {var subQ0=sQuery(id+"F22.wireOp",EDGE,"E59");var subQ1=sQuery(id+"F17.wireOp",EDGE,"E45.left");var subQ2=sQuery(id+"F17.wireOp",EDGE,"E45.top");var subQ3=makeQuery(id+"F19.opExtrude","SWEPT_EDGE",EDGE,{"disambiguationData":[OSD([subQ2,subQ1])]});var subQ4=makeQuery(id+"F22.imprint","INTERSECT",VERTEX,{"derivedFrom":[subQ3,subQ0]});Q1=makeQuery(id+"F22.imprint","IMPRINT",FACE,{"disambiguationData":[TD([[makeQuery(id+"F22.imprint","IMPRINT",EDGE,{"disambiguationData":[TD([[subQ4,-1.0]])],"derivedFrom":subQ0}),-1.0]])]});}
            var Q2;
            Q2=makeQuery(id+"F22.imprint","IMPRINT",FACE,{"disambiguationData":[TD([[makeQuery(id+"F22.imprint","IMPRINT",EDGE,{"derivedFrom":sQuery(id+"F22.wireOp",EDGE,"E60")}),1.0]])]});
            extrude(context, id + "F23", {"entities" : qUnion([Q0, Q1, Q2]), "operationType" : NewBodyOperationType.REMOVE, "oppositeDirection" : true, "depth" : 25 * mm, "offsetDistance" : 25 * mm});
        }
        {
            var Q0;
            Q0=makeQuery(id+"F19.opExtrude","SWEPT_FACE",FACE,{"disambiguationData":[OSD([sQuery(id+"F17.wireOp",EDGE,"E45.bottom"),sQuery(id+"F17.wireOp",EDGE,"E45.top"),sQuery(id+"F17.wireOp",EDGE,"E45.left")])]});
            var sketch = newSketch(context, id + "F24", { "sketchPlane" : qUnion([Q0])});
            skCircle(sketch, "E61", {"center": v(-15.14, 84.5) * mm, "radius": 4.04 * mm, "construction": true});
            skLineSegment(sketch, "E62", {"start": v(-17.16, 88) * mm, "end": v(-13.12, 88) * mm});
            skLineSegment(sketch, "E63", {"start": v(-13.12, 88) * mm, "end": v(-11.1, 84.5) * mm});
            skLineSegment(sketch, "E64", {"start": v(-11.1, 84.5) * mm, "end": v(-13.12, 81) * mm});
            skLineSegment(sketch, "E65", {"start": v(-13.12, 81) * mm, "end": v(-17.16, 81) * mm});
            skLineSegment(sketch, "E66", {"start": v(-17.16, 81) * mm, "end": v(-19.18, 84.5) * mm});
            skLineSegment(sketch, "E67", {"start": v(-19.18, 84.5) * mm, "end": v(-17.16, 88) * mm});
            skSolve(sketch);
        }
        {
            var Q0;
            Q0=makeQuery(id+"F24.imprint","IMPRINT",FACE,{"disambiguationData":[TD([[makeQuery(id+"F24.imprint","IMPRINT",EDGE,{"derivedFrom":sQuery(id+"F24.wireOp",EDGE,"E62")}),-1.0]])]});
            extrude(context, id + "F25", {"entities" : qUnion([Q0]), "operationType" : NewBodyOperationType.REMOVE, "oppositeDirection" : true, "depth" : 2.75 * mm, "offsetDistance" : 25 * mm});
        }
        {
            var Q0;
            {var subQ0=sQuery(id+"F17.wireOp",EDGE,"E45.left");var subQ1=sQuery(id+"F17.wireOp",EDGE,"E45.top");var subQ2=sQuery(id+"F17.wireOp",EDGE,"E45.bottom");Q0=makeQuery(id+"F19.boolean.opBoolean","MERGE",EDGE,{"derivedFrom":[makeQuery(id+"F18.opLoft","MID_CAP_EDGE",EDGE,{"disambiguationData":[OSD([subQ2,subQ1,subQ0])],"capPos":1.0}),makeQuery(id+"F19.opExtrude","CAP_EDGE",EDGE,{"disambiguationData":[OSD([subQ2,subQ1,subQ0])],"isStart":true})]});}
            var Q1;
            {var subQ0=sQuery(id+"F17.wireOp",EDGE,"E45.right");var subQ1=sQuery(id+"F17.wireOp",EDGE,"E45.left");var subQ2=sQuery(id+"F17.wireOp",EDGE,"E45.top");Q1=makeQuery(id+"F19.boolean.opBoolean","MERGE",EDGE,{"derivedFrom":[makeQuery(id+"F18.opLoft","MID_CAP_EDGE",EDGE,{"disambiguationData":[OSD([subQ2,subQ1,subQ0])],"capPos":1.0}),makeQuery(id+"F19.opExtrude","CAP_EDGE",EDGE,{"disambiguationData":[OSD([subQ2,subQ1,subQ0])],"isStart":true})]});}
            var Q2;
            {var subQ0=sQuery(id+"F17.wireOp",EDGE,"E45.right");var subQ1=sQuery(id+"F17.wireOp",EDGE,"E45.top");var subQ2=sQuery(id+"F17.wireOp",EDGE,"E45.bottom");Q2=makeQuery(id+"F19.boolean.opBoolean","MERGE",EDGE,{"derivedFrom":[makeQuery(id+"F18.opLoft","MID_CAP_EDGE",EDGE,{"disambiguationData":[OSD([subQ2,subQ1,subQ0])],"capPos":1.0}),makeQuery(id+"F19.opExtrude","CAP_EDGE",EDGE,{"disambiguationData":[OSD([subQ2,subQ1,subQ0])],"isStart":true})]});}
            var Q3;
            {var subQ0=sQuery(id+"F17.wireOp",EDGE,"E45.right");var subQ1=sQuery(id+"F17.wireOp",EDGE,"E45.bottom");var subQ2=sQuery(id+"F8.wireOp",EDGE,"E30.right");var subQ3=sQuery(id+"F8.wireOp",EDGE,"E30.bottom");Q3=makeQuery(id+"F19.boolean.opBoolean","MERGE",EDGE,{"derivedFrom":[makeQuery(id+"F18.opLoft","MID_CAP_EDGE",EDGE,{"disambiguationData":[OSD([subQ3,subQ2,subQ1,subQ0])],"capPos":1.0}),makeQuery(id+"F19.opExtrude","CAP_EDGE",EDGE,{"disambiguationData":[OSD([subQ3,subQ2,subQ1,sQuery(id+"F17.wireOp",EDGE,"E45.left"),subQ0])],"isStart":true})]});}
            var Q4;
            {var subQ0=sQuery(id+"F8.wireOp",EDGE,"E30.bottom");Q4=makeQuery(id+"F18.boolean.opBoolean","MERGE",EDGE,{"derivedFrom":[makeQuery(id+"F9.opExtrude","CAP_EDGE",EDGE,{"disambiguationData":[OSD([subQ0])],"isStart":false}),makeQuery(id+"F18.opLoft","MID_CAP_EDGE",EDGE,{"disambiguationData":[OSD([sQuery(id+"F8.wireOp",EDGE,"E29.sketch_text.stroke-2"),subQ0,sQuery(id+"F8.wireOp",EDGE,"E30.right")])],"capPos":0.0})]});}
            var Q5;
            {var subQ0=sQuery(id+"F8.wireOp",EDGE,"E30.right");Q5=makeQuery(id+"F18.boolean.opBoolean","MERGE",EDGE,{"derivedFrom":[makeQuery(id+"F9.opExtrude","CAP_EDGE",EDGE,{"disambiguationData":[OSD([subQ0])],"isStart":false}),makeQuery(id+"F18.opLoft","MID_CAP_EDGE",EDGE,{"disambiguationData":[OSD([sQuery(id+"F8.wireOp",EDGE,"E30.bottom"),sQuery(id+"F8.wireOp",EDGE,"E30.top"),subQ0])],"capPos":0.0})]});}
            var Q6;
            {var subQ0=sQuery(id+"F8.wireOp",EDGE,"E30.top");var subQ1=makeQuery(id+"F9.opExtrude","CAP_EDGE",EDGE,{"disambiguationData":[OSD([subQ0])],"isStart":false});var subQ2=sQuery(id+"F11.wireOp",EDGE,"E35");var subQ3=sQuery(id+"F8.wireOp",EDGE,"E30.right");var subQ4=sQuery(id+"F8.wireOp",EDGE,"E30.left");var subQ5=sQuery(id+"F8.wireOp",EDGE,"E30.bottom");var subQ6=sQuery(id+"F8.wireOp",EDGE,"E29.sketch_text.stroke-26");var subQ7=sQuery(id+"F8.wireOp",EDGE,"E29.sketch_text.stroke-25");var subQ8=sQuery(id+"F8.wireOp",EDGE,"E29.sketch_text.stroke-24");var subQ9=sQuery(id+"F8.wireOp",EDGE,"E29.sketch_text.stroke-23");var subQ10=sQuery(id+"F8.wireOp",EDGE,"E29.sketch_text.stroke-22");var subQ11=sQuery(id+"F8.wireOp",EDGE,"E29.sketch_text.stroke-21");var subQ12=sQuery(id+"F8.wireOp",EDGE,"E29.sketch_text.stroke-20");var subQ13=sQuery(id+"F8.wireOp",EDGE,"E29.sketch_text.stroke-19");var subQ14=sQuery(id+"F8.wireOp",EDGE,"E29.sketch_text.stroke-18");var subQ15=sQuery(id+"F8.wireOp",EDGE,"E29.sketch_text.stroke-17");var subQ16=sQuery(id+"F8.wireOp",EDGE,"E29.sketch_text.stroke-16");var subQ17=sQuery(id+"F8.wireOp",EDGE,"E29.sketch_text.stroke-15");var subQ18=sQuery(id+"F8.wireOp",EDGE,"E29.sketch_text.stroke-10");var subQ19=sQuery(id+"F8.wireOp",EDGE,"E29.sketch_text.stroke-9");var subQ20=sQuery(id+"F8.wireOp",EDGE,"E29.sketch_text.stroke-8");var subQ21=sQuery(id+"F8.wireOp",EDGE,"E29.sketch_text.stroke-7");var subQ22=sQuery(id+"F8.wireOp",EDGE,"E29.sketch_text.stroke-6");var subQ23=sQuery(id+"F8.wireOp",EDGE,"E29.sketch_text.stroke-5");var subQ24=sQuery(id+"F8.wireOp",EDGE,"E29.sketch_text.stroke-2");var subQ25=sQuery(id+"F8.wireOp",EDGE,"E29.sketch_text.stroke-1");var subQ26=sQuery(id+"F8.wireOp",EDGE,"E28.sketch_text.stroke-11");var subQ27=sQuery(id+"F8.wireOp",EDGE,"E28.sketch_text.stroke-10");var subQ28=sQuery(id+"F8.wireOp",EDGE,"E28.sketch_text.stroke-9");var subQ29=sQuery(id+"F8.wireOp",EDGE,"E28.sketch_text.stroke-8");var subQ30=sQuery(id+"F8.wireOp",EDGE,"E28.sketch_text.stroke-7");var subQ31=sQuery(id+"F8.wireOp",EDGE,"E28.sketch_text.stroke-6");var subQ32=sQuery(id+"F8.wireOp",EDGE,"E28.sketch_text.stroke-5");var subQ33=sQuery(id+"F8.wireOp",EDGE,"E28.sketch_text.stroke-4");var subQ34=sQuery(id+"F8.wireOp",EDGE,"E28.sketch_text.stroke-3");var subQ35=sQuery(id+"F8.wireOp",EDGE,"E28.sketch_text.stroke-2");var subQ36=sQuery(id+"F8.wireOp",EDGE,"E28.sketch_text.stroke-1");var subQ37=sQuery(id+"F8.wireOp",EDGE,"E28.sketch_text.stroke-0");var subQ38=sQuery(id+"F8.wireOp",EDGE,"E27.sketch_text.stroke-18");var subQ39=sQuery(id+"F8.wireOp",EDGE,"E27.sketch_text.stroke-17");var subQ40=sQuery(id+"F8.wireOp",EDGE,"E27.sketch_text.stroke-16");var subQ41=sQuery(id+"F8.wireOp",EDGE,"E27.sketch_text.stroke-15");var subQ42=sQuery(id+"F8.wireOp",EDGE,"E27.sketch_text.stroke-14");var subQ43=sQuery(id+"F8.wireOp",EDGE,"E27.sketch_text.stroke-13");var subQ44=sQuery(id+"F8.wireOp",EDGE,"E27.sketch_text.stroke-12");var subQ45=sQuery(id+"F8.wireOp",EDGE,"E27.sketch_text.stroke-11");var subQ46=sQuery(id+"F8.wireOp",EDGE,"E27.sketch_text.stroke-10");var subQ47=sQuery(id+"F8.wireOp",EDGE,"E27.sketch_text.stroke-9");var subQ48=sQuery(id+"F8.wireOp",EDGE,"E27.sketch_text.stroke-8");var subQ49=sQuery(id+"F8.wireOp",EDGE,"E27.sketch_text.stroke-7");var subQ50=sQuery(id+"F8.wireOp",EDGE,"E27.sketch_text.stroke-6");var subQ51=sQuery(id+"F8.wireOp",EDGE,"E27.sketch_text.stroke-5");var subQ52=sQuery(id+"F8.wireOp",EDGE,"E27.sketch_text.stroke-4");var subQ53=sQuery(id+"F8.wireOp",EDGE,"E27.sketch_text.stroke-3");var subQ54=sQuery(id+"F8.wireOp",EDGE,"E27.sketch_text.stroke-2");var subQ55=sQuery(id+"F8.wireOp",EDGE,"E27.sketch_text.stroke-1");var subQ56=sQuery(id+"F8.wireOp",EDGE,"E27.sketch_text.stroke-0");Q6=makeQuery(id+"F18.boolean.opBoolean","MERGE",EDGE,{"derivedFrom":[subQ1,makeQuery(id+"F18.opLoft","MID_CAP_EDGE",EDGE,{"disambiguationData":[OSD([subQ56,subQ55,subQ54,subQ53,subQ52,subQ51,subQ50,subQ49,subQ48,subQ47,subQ46,subQ45,subQ44,subQ43,subQ42,subQ41,subQ40,subQ39,subQ38,subQ37,subQ36,subQ35,subQ34,subQ33,subQ32,subQ31,subQ30,subQ29,subQ28,subQ27,subQ26,subQ25,subQ24,subQ23,subQ22,subQ21,subQ20,subQ19,subQ18,subQ17,subQ16,subQ15,subQ14,subQ13,subQ12,subQ11,subQ10,subQ9,subQ8,subQ7,subQ6,subQ5,subQ0,subQ4,subQ3,subQ2]),TDD([makeQuery(id+"F16.imprint","INTERSECT",VERTEX,{"derivedFrom":[makeQuery(id+"F9.opExtrude","CAP_EDGE",EDGE,{"disambiguationData":[OSD([subQ3])],"isStart":false}),subQ1]}),makeQuery(id+"F16.imprint","INTERSECT",VERTEX,{"derivedFrom":[subQ1,makeQuery(id+"F13.boolean.opBoolean","INTERSECT",EDGE,{"derivedFrom":[makeQuery(id+"F9.opExtrude","CAP_FACE",FACE,{"disambiguationData":[OSD([subQ56,subQ55,subQ54,subQ53,subQ52,subQ51,subQ50,subQ49,subQ48,subQ47,subQ46,subQ45,subQ44,subQ43,subQ42,subQ41,subQ40,subQ39,subQ38,subQ37,subQ36,subQ35,subQ34,subQ33,subQ32,subQ31,subQ30,subQ29,subQ28,subQ27,subQ26,subQ25,subQ24,subQ23,subQ22,subQ21,subQ20,subQ19,subQ18,subQ17,subQ16,subQ15,subQ14,subQ13,subQ12,subQ11,subQ10,subQ9,subQ8,subQ7,subQ6,subQ5,subQ0,subQ4,subQ3])],"isStart":false}),makeQuery(id+"F13.opExtrude","SWEPT_FACE",FACE,{"disambiguationData":[OSD([subQ2])]})]})]}),makeQuery(id+"F16.imprint","IMPRINT",EDGE,{"derivedFrom":subQ1})])],"capPos":0.0})]});}
            var Q7;
            {var subQ0=sQuery(id+"F11.wireOp",EDGE,"E35");var subQ1=sQuery(id+"F8.wireOp",EDGE,"E30.right");var subQ2=sQuery(id+"F8.wireOp",EDGE,"E30.left");var subQ3=sQuery(id+"F8.wireOp",EDGE,"E30.top");var subQ4=sQuery(id+"F8.wireOp",EDGE,"E30.bottom");var subQ5=sQuery(id+"F8.wireOp",EDGE,"E29.sketch_text.stroke-26");var subQ6=sQuery(id+"F8.wireOp",EDGE,"E29.sketch_text.stroke-25");var subQ7=sQuery(id+"F8.wireOp",EDGE,"E29.sketch_text.stroke-24");var subQ8=sQuery(id+"F8.wireOp",EDGE,"E29.sketch_text.stroke-23");var subQ9=sQuery(id+"F8.wireOp",EDGE,"E29.sketch_text.stroke-22");var subQ10=sQuery(id+"F8.wireOp",EDGE,"E29.sketch_text.stroke-21");var subQ11=sQuery(id+"F8.wireOp",EDGE,"E29.sketch_text.stroke-20");var subQ12=sQuery(id+"F8.wireOp",EDGE,"E29.sketch_text.stroke-19");var subQ13=sQuery(id+"F8.wireOp",EDGE,"E29.sketch_text.stroke-18");var subQ14=sQuery(id+"F8.wireOp",EDGE,"E29.sketch_text.stroke-17");var subQ15=sQuery(id+"F8.wireOp",EDGE,"E29.sketch_text.stroke-16");var subQ16=sQuery(id+"F8.wireOp",EDGE,"E29.sketch_text.stroke-15");var subQ17=sQuery(id+"F8.wireOp",EDGE,"E29.sketch_text.stroke-10");var subQ18=sQuery(id+"F8.wireOp",EDGE,"E29.sketch_text.stroke-9");var subQ19=sQuery(id+"F8.wireOp",EDGE,"E29.sketch_text.stroke-8");var subQ20=sQuery(id+"F8.wireOp",EDGE,"E29.sketch_text.stroke-7");var subQ21=sQuery(id+"F8.wireOp",EDGE,"E29.sketch_text.stroke-6");var subQ22=sQuery(id+"F8.wireOp",EDGE,"E29.sketch_text.stroke-5");var subQ23=sQuery(id+"F8.wireOp",EDGE,"E29.sketch_text.stroke-2");var subQ24=sQuery(id+"F8.wireOp",EDGE,"E29.sketch_text.stroke-1");var subQ25=sQuery(id+"F8.wireOp",EDGE,"E28.sketch_text.stroke-11");var subQ26=sQuery(id+"F8.wireOp",EDGE,"E28.sketch_text.stroke-10");var subQ27=sQuery(id+"F8.wireOp",EDGE,"E28.sketch_text.stroke-9");var subQ28=sQuery(id+"F8.wireOp",EDGE,"E28.sketch_text.stroke-8");var subQ29=sQuery(id+"F8.wireOp",EDGE,"E28.sketch_text.stroke-7");var subQ30=sQuery(id+"F8.wireOp",EDGE,"E28.sketch_text.stroke-6");var subQ31=sQuery(id+"F8.wireOp",EDGE,"E28.sketch_text.stroke-5");var subQ32=sQuery(id+"F8.wireOp",EDGE,"E28.sketch_text.stroke-4");var subQ33=sQuery(id+"F8.wireOp",EDGE,"E28.sketch_text.stroke-3");var subQ34=sQuery(id+"F8.wireOp",EDGE,"E28.sketch_text.stroke-2");var subQ35=sQuery(id+"F8.wireOp",EDGE,"E28.sketch_text.stroke-1");var subQ36=sQuery(id+"F8.wireOp",EDGE,"E28.sketch_text.stroke-0");var subQ37=sQuery(id+"F8.wireOp",EDGE,"E27.sketch_text.stroke-18");var subQ38=sQuery(id+"F8.wireOp",EDGE,"E27.sketch_text.stroke-17");var subQ39=sQuery(id+"F8.wireOp",EDGE,"E27.sketch_text.stroke-16");var subQ40=sQuery(id+"F8.wireOp",EDGE,"E27.sketch_text.stroke-15");var subQ41=sQuery(id+"F8.wireOp",EDGE,"E27.sketch_text.stroke-14");var subQ42=sQuery(id+"F8.wireOp",EDGE,"E27.sketch_text.stroke-13");var subQ43=sQuery(id+"F8.wireOp",EDGE,"E27.sketch_text.stroke-12");var subQ44=sQuery(id+"F8.wireOp",EDGE,"E27.sketch_text.stroke-11");var subQ45=sQuery(id+"F8.wireOp",EDGE,"E27.sketch_text.stroke-10");var subQ46=sQuery(id+"F8.wireOp",EDGE,"E27.sketch_text.stroke-9");var subQ47=sQuery(id+"F8.wireOp",EDGE,"E27.sketch_text.stroke-8");var subQ48=sQuery(id+"F8.wireOp",EDGE,"E27.sketch_text.stroke-7");var subQ49=sQuery(id+"F8.wireOp",EDGE,"E27.sketch_text.stroke-6");var subQ50=sQuery(id+"F8.wireOp",EDGE,"E27.sketch_text.stroke-5");var subQ51=sQuery(id+"F8.wireOp",EDGE,"E27.sketch_text.stroke-4");var subQ52=sQuery(id+"F8.wireOp",EDGE,"E27.sketch_text.stroke-3");var subQ53=sQuery(id+"F8.wireOp",EDGE,"E27.sketch_text.stroke-2");var subQ54=sQuery(id+"F8.wireOp",EDGE,"E27.sketch_text.stroke-1");var subQ55=sQuery(id+"F8.wireOp",EDGE,"E27.sketch_text.stroke-0");var subQ56=makeQuery(id+"F13.boolean.opBoolean","INTERSECT",EDGE,{"derivedFrom":[makeQuery(id+"F9.opExtrude","CAP_FACE",FACE,{"disambiguationData":[OSD([subQ55,subQ54,subQ53,subQ52,subQ51,subQ50,subQ49,subQ48,subQ47,subQ46,subQ45,subQ44,subQ43,subQ42,subQ41,subQ40,subQ39,subQ38,subQ37,subQ36,subQ35,subQ34,subQ33,subQ32,subQ31,subQ30,subQ29,subQ28,subQ27,subQ26,subQ25,subQ24,subQ23,subQ22,subQ21,subQ20,subQ19,subQ18,subQ17,subQ16,subQ15,subQ14,subQ13,subQ12,subQ11,subQ10,subQ9,subQ8,subQ7,subQ6,subQ5,subQ4,subQ3,subQ2,subQ1])],"isStart":false}),makeQuery(id+"F13.opExtrude","SWEPT_FACE",FACE,{"disambiguationData":[OSD([subQ0])]})]});Q7=makeQuery(id+"F18.boolean.opBoolean","MERGE",EDGE,{"derivedFrom":[subQ56,makeQuery(id+"F18.opLoft","MID_CAP_EDGE",EDGE,{"disambiguationData":[OSD([subQ55,subQ54,subQ53,subQ52,subQ51,subQ50,subQ49,subQ48,subQ47,subQ46,subQ45,subQ44,subQ43,subQ42,subQ41,subQ40,subQ39,subQ38,subQ37,subQ36,subQ35,subQ34,subQ33,subQ32,subQ31,subQ30,subQ29,subQ28,subQ27,subQ26,subQ25,subQ24,subQ23,subQ22,subQ21,subQ20,subQ19,subQ18,subQ17,subQ16,subQ15,subQ14,subQ13,subQ12,subQ11,subQ10,subQ9,subQ8,subQ7,subQ6,subQ5,subQ4,subQ3,subQ2,subQ1,subQ0]),TDD([makeQuery(id+"F16.imprint","INTERSECT",VERTEX,{"derivedFrom":[makeQuery(id+"F9.opExtrude","CAP_EDGE",EDGE,{"disambiguationData":[OSD([subQ3])],"isStart":false}),subQ56]}),makeQuery(id+"F16.imprint","INTERSECT",VERTEX,{"derivedFrom":[makeQuery(id+"F9.opExtrude","CAP_EDGE",EDGE,{"disambiguationData":[OSD([subQ23])],"isStart":false}),subQ56]}),makeQuery(id+"F16.imprint","IMPRINT",EDGE,{"derivedFrom":subQ56})])],"capPos":0.0})]});}
            fillet(context, id + "F26", {"entities" : qUnion([Q0, Q1, Q2, Q3, Q4, Q5, Q6, Q7]), "tangentPropagation" : true, "radius" : 3 * mm, "defaultsChanged" : false, "vertexSettings" : [], "allowEdgeOverflow" : false});
        }
    });
